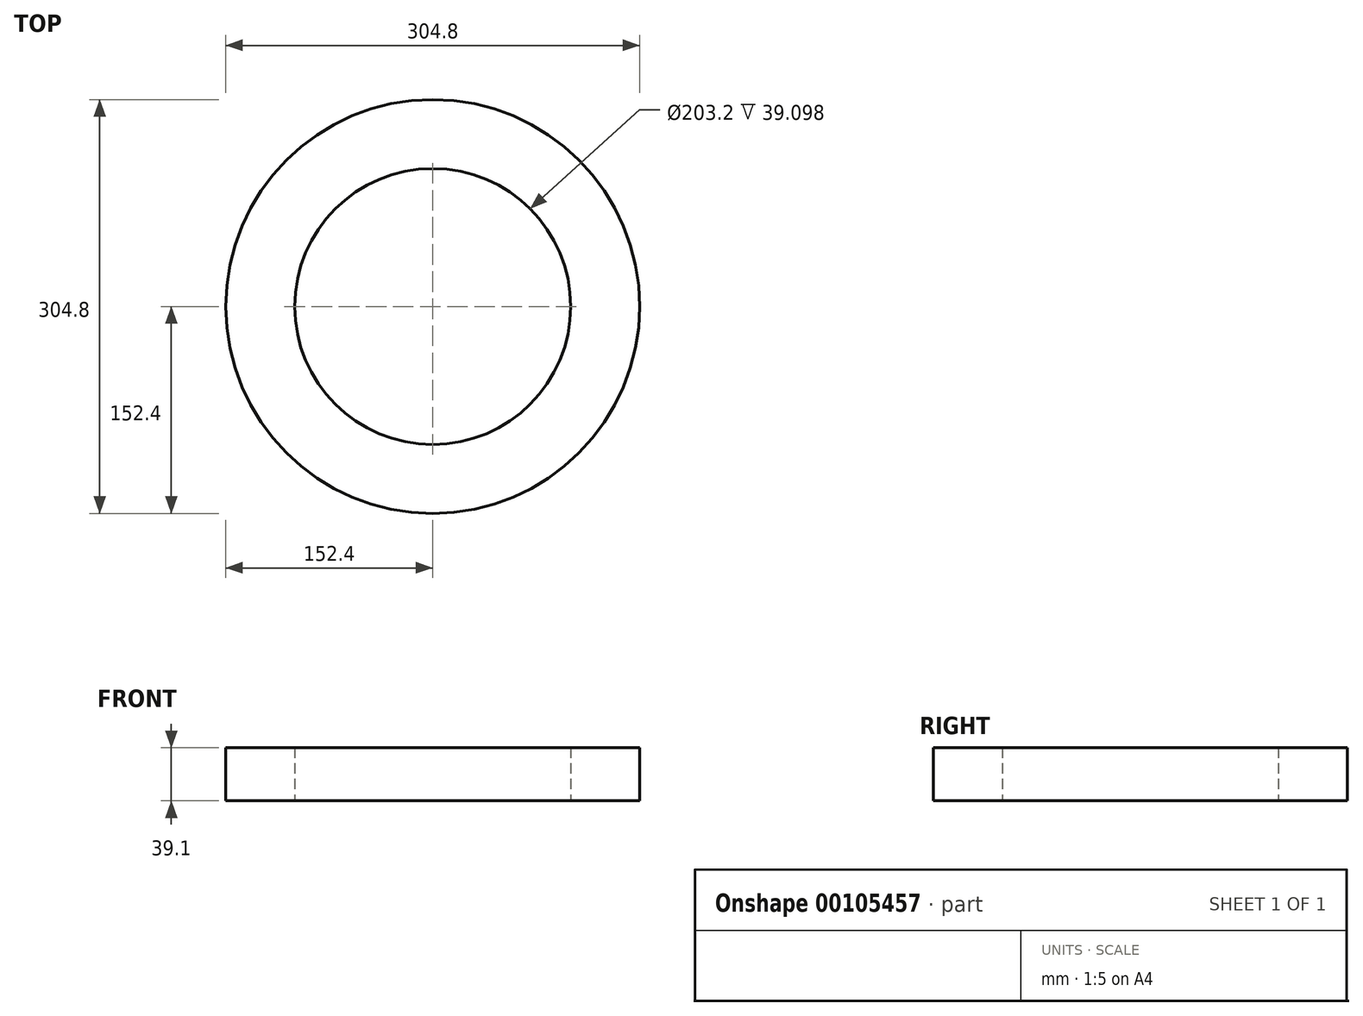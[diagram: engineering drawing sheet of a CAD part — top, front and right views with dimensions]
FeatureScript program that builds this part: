
annotation { "Feature Type Name" : "Feature", "Feature Type Description" : "" }
export const myFeature = defineFeature(function(context is Context, id is Id, definition is map)
    precondition{}
    {
        {
            var Q0;
            Q0=qCreatedBy(makeId("Top.planeOp"),FACE);
            var sketch = newSketch(context, id + "F0", { "sketchPlane" : qUnion([Q0])});
            skCircle(sketch, "E0", {"center": v(0, 0) * mm, "radius": 152.4 * mm});
            skCircle(sketch, "E1", {"center": v(0, 0) * mm, "radius": 101.6 * mm});
            skSolve(sketch);
        }
        {
            var Q0;
            Q0 = qSketchRegion(id + "F0", true);
            extrude(context, id + "F1", {"entities" : qUnion([Q0]), "depth" : 39.1 * mm});
        }
    });
